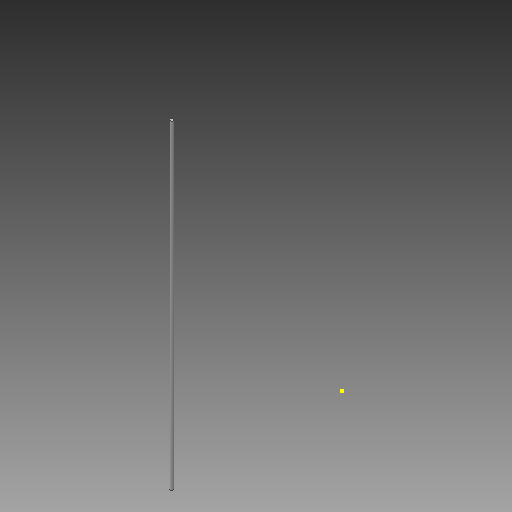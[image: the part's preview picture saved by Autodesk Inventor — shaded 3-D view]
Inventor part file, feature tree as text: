
AUTODESK INVENTOR PART (.ipt)
format: ipt  version: 2018 (Build 220112000, 112)  size: 95,744 bytes
history: native  units: mm
features: sketch x2, extrude x1, thread x1
ambient origin geometry x8: Origin, YZ Plane, XZ Plane, XY Plane, X Axis, Y Axis, Z Axis, Center Point
bodies: Solid1 (feature_tree)
feature tree (4):
  sketch  "Sketch1"  dims[d0=8.0mm d1=800.0mm d2=0.0mm d3=10.0mm d4=0.0mm]
  extrude  "Extrusion1"  Depth=800.0mm TaperAngle=0.0deg
  thread  "Thread1"  [1 undecoded]
  sketch  "Sketch2"
note: 1 required parameter value undecoded (feature->parameter linkage not recoverable at this tier; creation-order binding heuristic only, values carry confidence <= 0.55)
